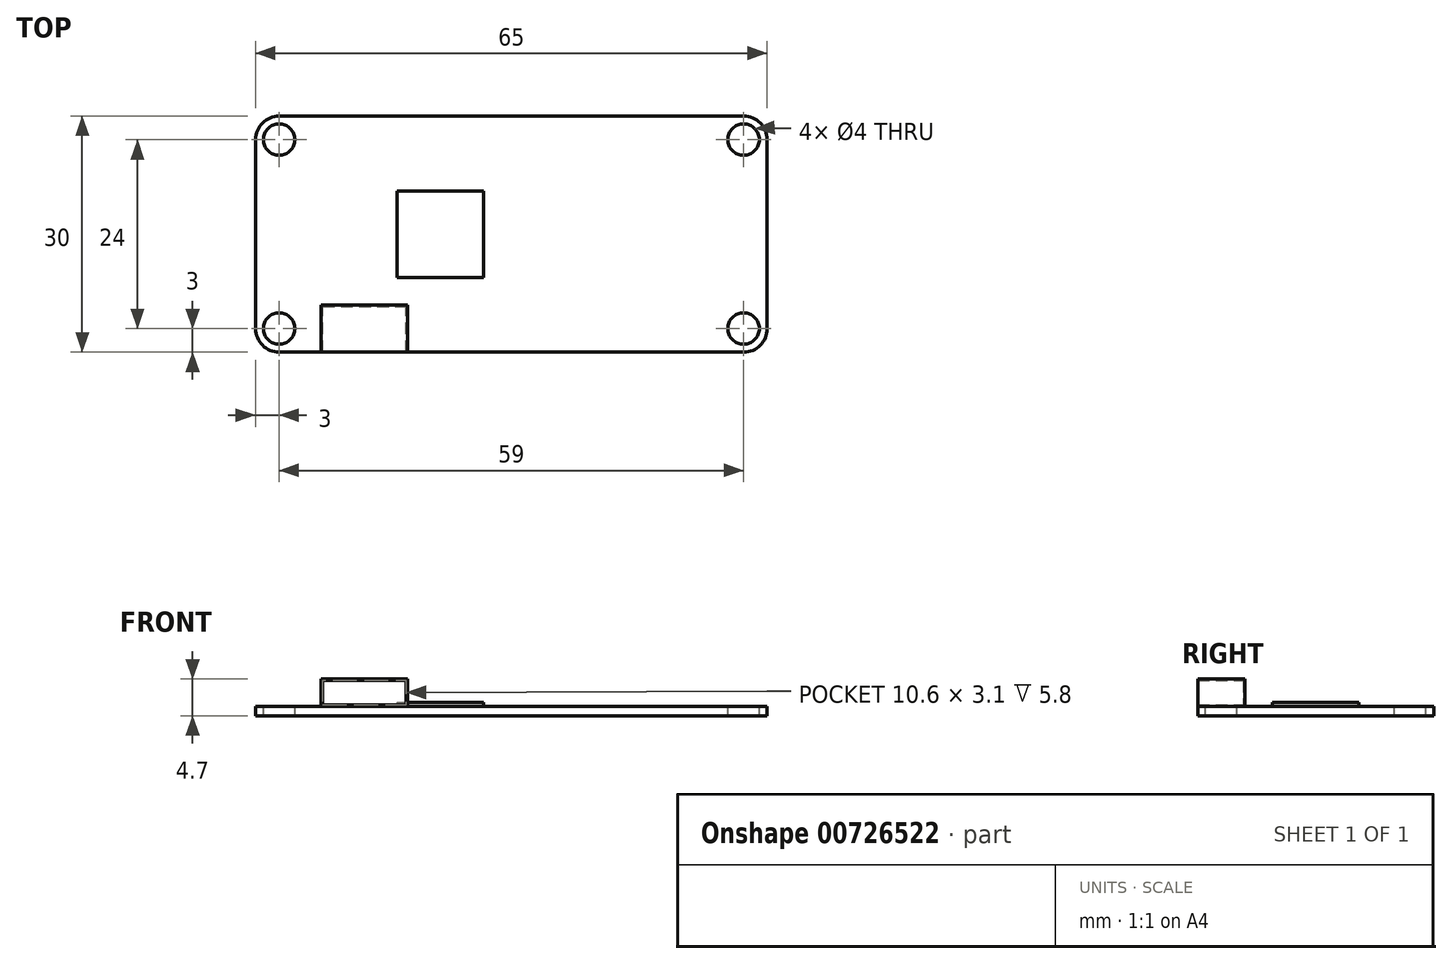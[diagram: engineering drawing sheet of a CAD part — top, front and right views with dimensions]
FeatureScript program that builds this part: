
annotation { "Feature Type Name" : "Feature", "Feature Type Description" : "" }
export const myFeature = defineFeature(function(context is Context, id is Id, definition is map)
    precondition{}
    {
        {
            var Q0;
            Q0=qCreatedBy(makeId("Top.planeOp"),FACE);
            var sketch = newSketch(context, id + "F0", { "sketchPlane" : qUnion([Q0])});
            skLineSegment(sketch, "E0.bottom", {"start": v(29.5, 15) * mm, "end": v(-29.5, 15) * mm});
            skLineSegment(sketch, "E0.top", {"start": v(29.5, -15) * mm, "end": v(-29.5, -15) * mm});
            skLineSegment(sketch, "E0.left", {"start": v(32.5, 12) * mm, "end": v(32.5, -12) * mm});
            skLineSegment(sketch, "E0.right", {"start": v(-32.5, 12) * mm, "end": v(-32.5, -12) * mm});
            skPoint(sketch, "E0.middle", {"position": v(0, 0) * mm});
            skPoint(sketch, "E1.visualSharp", {"position": v(-32.5, 15) * mm});
            skArc(sketch, "E1.filletArc", {"start": v(-29.5, 15) * mm, "mid": v(-31.62, 14.12) * mm, "end": v(-32.5, 12) * mm});
            skPoint(sketch, "E2.visualSharp", {"position": v(-32.5, -15) * mm});
            skArc(sketch, "E2.filletArc", {"start": v(-32.5, -12) * mm, "mid": v(-31.62, -14.12) * mm, "end": v(-29.5, -15) * mm});
            skPoint(sketch, "E3.visualSharp", {"position": v(32.5, -15) * mm});
            skArc(sketch, "E3.filletArc", {"start": v(29.5, -15) * mm, "mid": v(31.62, -14.12) * mm, "end": v(32.5, -12) * mm});
            skPoint(sketch, "E4.visualSharp", {"position": v(32.5, 15) * mm});
            skArc(sketch, "E4.filletArc", {"start": v(32.5, 12) * mm, "mid": v(31.62, 14.12) * mm, "end": v(29.5, 15) * mm});
            skSolve(sketch);
        }
        {
            var Q0;
            Q0 = qSketchRegion(id + "F0", true);
            extrude(context, id + "F1", {"entities" : qUnion([Q0]), "depth" : 1.2 * mm, "offsetDistance" : 25 * mm});
        }
        {
            var Q0;
            Q0=makeQuery(id+"F1.opExtrude","CAP_FACE",FACE,{"disambiguationData":[OSD([sQuery(id+"F0.wireOp",EDGE,"E0.bottom"),sQuery(id+"F0.wireOp",EDGE,"E0.top"),sQuery(id+"F0.wireOp",EDGE,"E0.left"),sQuery(id+"F0.wireOp",EDGE,"E0.right"),sQuery(id+"F0.wireOp",EDGE,"E1.filletArc"),sQuery(id+"F0.wireOp",EDGE,"E2.filletArc"),sQuery(id+"F0.wireOp",EDGE,"E3.filletArc"),sQuery(id+"F0.wireOp",EDGE,"E4.filletArc")])],"isStart":false});
            var sketch = newSketch(context, id + "F2", { "sketchPlane" : qUnion([Q0])});
            skCircle(sketch, "E5", {"center": v(-29.5, 12) * mm, "radius": 2 * mm});
            skCircle(sketch, "E6.MirrorC", {"center": v(29.5, 12) * mm, "radius": 2 * mm});
            skCircle(sketch, "E7.MirrorC", {"center": v(-29.5, -12) * mm, "radius": 2 * mm});
            skCircle(sketch, "E8.MirrorC", {"center": v(29.5, -12) * mm, "radius": 2 * mm});
            skSolve(sketch);
        }
        {
            var Q0;
            Q0 = qSketchRegion(id + "F2", true);
            extrude(context, id + "F3", {"entities" : qUnion([Q0]), "operationType" : NewBodyOperationType.REMOVE, "oppositeDirection" : true, "depth" : 2 * mm, "offsetDistance" : 25 * mm});
        }
        {
            var Q0;
            Q0=makeQuery(id+"F1.opExtrude","CAP_FACE",FACE,{"disambiguationData":[OSD([sQuery(id+"F0.wireOp",EDGE,"E0.bottom"),sQuery(id+"F0.wireOp",EDGE,"E0.top"),sQuery(id+"F0.wireOp",EDGE,"E0.left"),sQuery(id+"F0.wireOp",EDGE,"E0.right"),sQuery(id+"F0.wireOp",EDGE,"E1.filletArc"),sQuery(id+"F0.wireOp",EDGE,"E2.filletArc"),sQuery(id+"F0.wireOp",EDGE,"E3.filletArc"),sQuery(id+"F0.wireOp",EDGE,"E4.filletArc")])],"isStart":false});
            var sketch = newSketch(context, id + "F4", { "sketchPlane" : qUnion([Q0])});
            skLineSegment(sketch, "E9.bottom", {"start": v(-14.5, 5.5) * mm, "end": v(-3.5, 5.5) * mm});
            skLineSegment(sketch, "E9.top", {"start": v(-14.5, -5.5) * mm, "end": v(-3.5, -5.5) * mm});
            skLineSegment(sketch, "E9.left", {"start": v(-14.5, 5.5) * mm, "end": v(-14.5, -5.5) * mm});
            skLineSegment(sketch, "E9.right", {"start": v(-3.5, 5.5) * mm, "end": v(-3.5, -5.5) * mm});
            skPoint(sketch, "E9.middle", {"position": v(-9, 0) * mm});
            skPoint(sketch, "E9.middle.positionSnap0", {"position": v(-32.5, 0) * mm});
            skPoint(sketch, "E9.centerSnap0", {"position": v(-32.5, 0) * mm});
            skSolve(sketch);
        }
        {
            var Q0;
            Q0 = qSketchRegion(id + "F4", true);
            extrude(context, id + "F5", {"entities" : qUnion([Q0]), "depth" : 0.5 * mm, "offsetDistance" : 25 * mm});
        }
        {
            var Q0;
            Q0=makeQuery(id+"F1.opExtrude","CAP_FACE",FACE,{"disambiguationData":[OSD([sQuery(id+"F0.wireOp",EDGE,"E0.bottom"),sQuery(id+"F0.wireOp",EDGE,"E0.top"),sQuery(id+"F0.wireOp",EDGE,"E0.left"),sQuery(id+"F0.wireOp",EDGE,"E0.right"),sQuery(id+"F0.wireOp",EDGE,"E1.filletArc"),sQuery(id+"F0.wireOp",EDGE,"E2.filletArc"),sQuery(id+"F0.wireOp",EDGE,"E3.filletArc"),sQuery(id+"F0.wireOp",EDGE,"E4.filletArc")])],"isStart":false});
            var sketch = newSketch(context, id + "F6", { "sketchPlane" : qUnion([Q0])});
            skLineSegment(sketch, "E10.bottom", {"start": v(-24.15, -15) * mm, "end": v(-13.15, -15) * mm});
            skLineSegment(sketch, "E10.top", {"start": v(-24.15, -9) * mm, "end": v(-13.15, -9) * mm});
            skLineSegment(sketch, "E10.left", {"start": v(-24.15, -15) * mm, "end": v(-24.15, -9) * mm});
            skLineSegment(sketch, "E10.right", {"start": v(-13.15, -15) * mm, "end": v(-13.15, -9) * mm});
            skSolve(sketch);
        }
        {
            var Q0;
            Q0=makeQuery(id+"F6.imprint","IMPRINT",FACE,{"disambiguationData":[TD([[makeQuery(id+"F6.imprint","IMPRINT",EDGE,{"derivedFrom":sQuery(id+"F6.wireOp",EDGE,"E10.bottom")}),-1.0]])]});
            extrude(context, id + "F7", {"entities" : qUnion([Q0]), "depth" : 3.5 * mm, "offsetDistance" : 25 * mm});
        }
        {
            var Q0;
            Q0=makeQuery(id+"F7.opExtrude","SWEPT_FACE",FACE,{"disambiguationData":[OSD([sQuery(id+"F6.wireOp",EDGE,"E10.bottom")])]});
            shell(context, id + "F8", {"entities" : qUnion([Q0]), "thickness" : 0.2 * mm});
        }
    });
